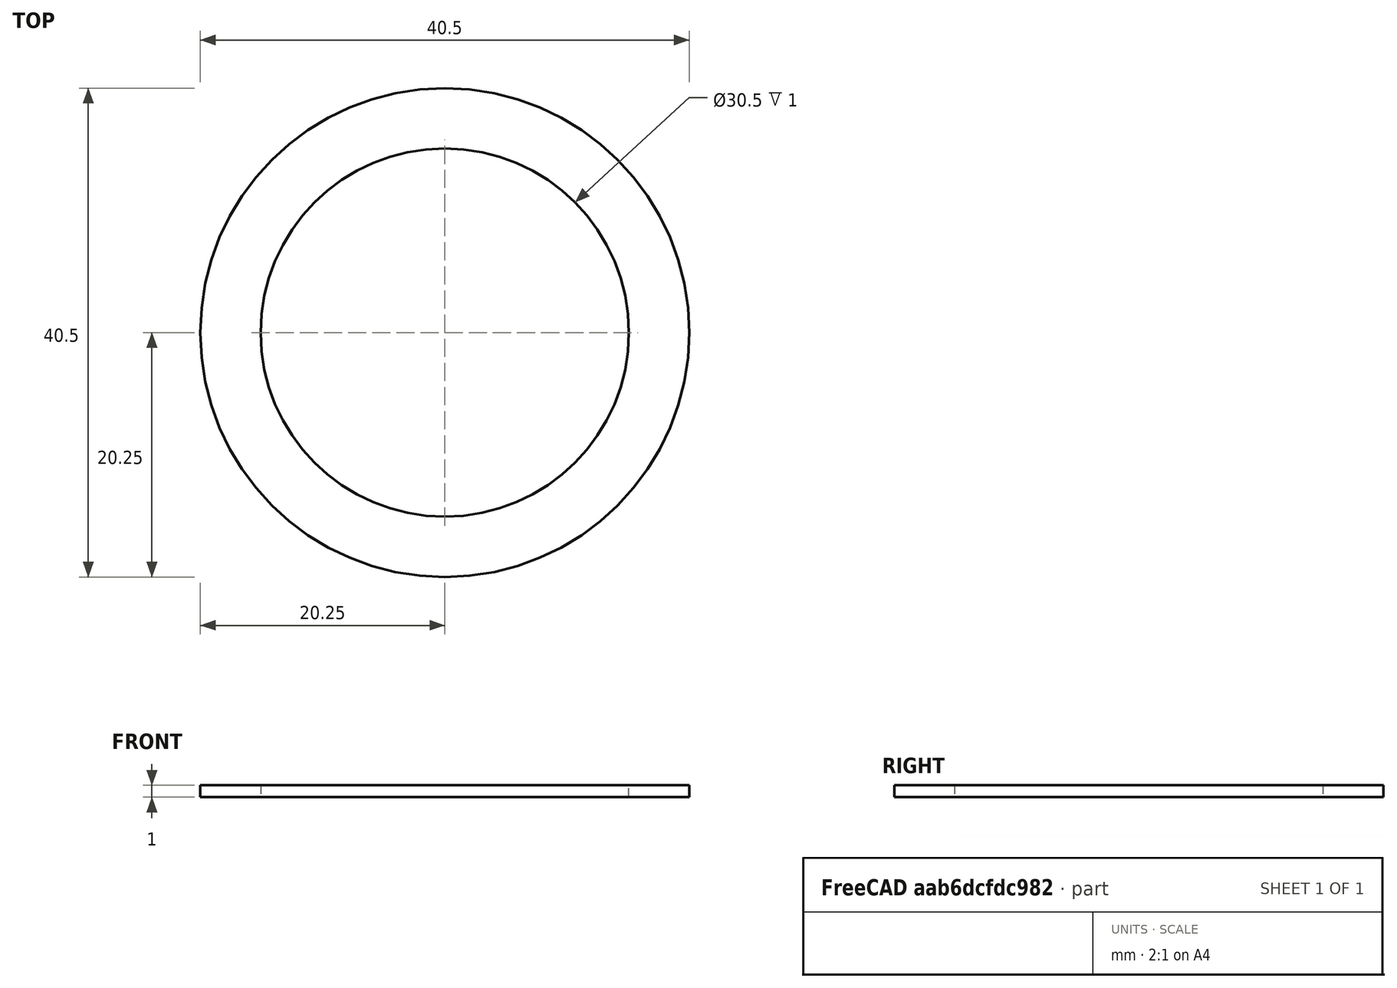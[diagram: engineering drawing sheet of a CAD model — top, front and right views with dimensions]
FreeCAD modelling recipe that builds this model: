
FCSTD DOCUMENT  (FreeCAD 0.18R16146 (Git))
Label: vp4012
License: All rights reserved
LicenseURL: http://en.wikipedia.org/wiki/All_rights_reserved
objects: Sketcher::SketchObject×1, PartDesign::Pad×1, PartDesign::Body×1
note: 4 computed .brp shape members not serialized (recipe doc carries the construction recipe); baked Part::Feature solids carry a one-line shape summary decoded from their .brp

FEATURE [Sketcher::SketchObject] Sketch
  MapMode = 5
  Support = -> [XY_Plane]
  sketch-geometry (2):
    g0: Circle CenterX=0 CenterY=0 CenterZ=0 NormalX=0 NormalY=0 NormalZ=1 AngleXU=0 Radius=15.25
    g1: Circle CenterX=0 CenterY=0 CenterZ=0 NormalX=0 NormalY=0 NormalZ=1 AngleXU=0 Radius=20.25
  constraints (4):
    c: Coincident(g0,g-1)
    c: Coincident(g1,g0)
    c: Diameter(g0) = 30.5
    c: Diameter(g1) = 40.5
FEATURE [PartDesign::Pad] Pad
  Length = 1
  Length2 = 100
  Profile = -> Sketch
  Type = 0
FEATURE [PartDesign::Body] Body
  Group = -> [Sketch,Pad]
  Origin = -> Origin
  Tip = -> Pad
